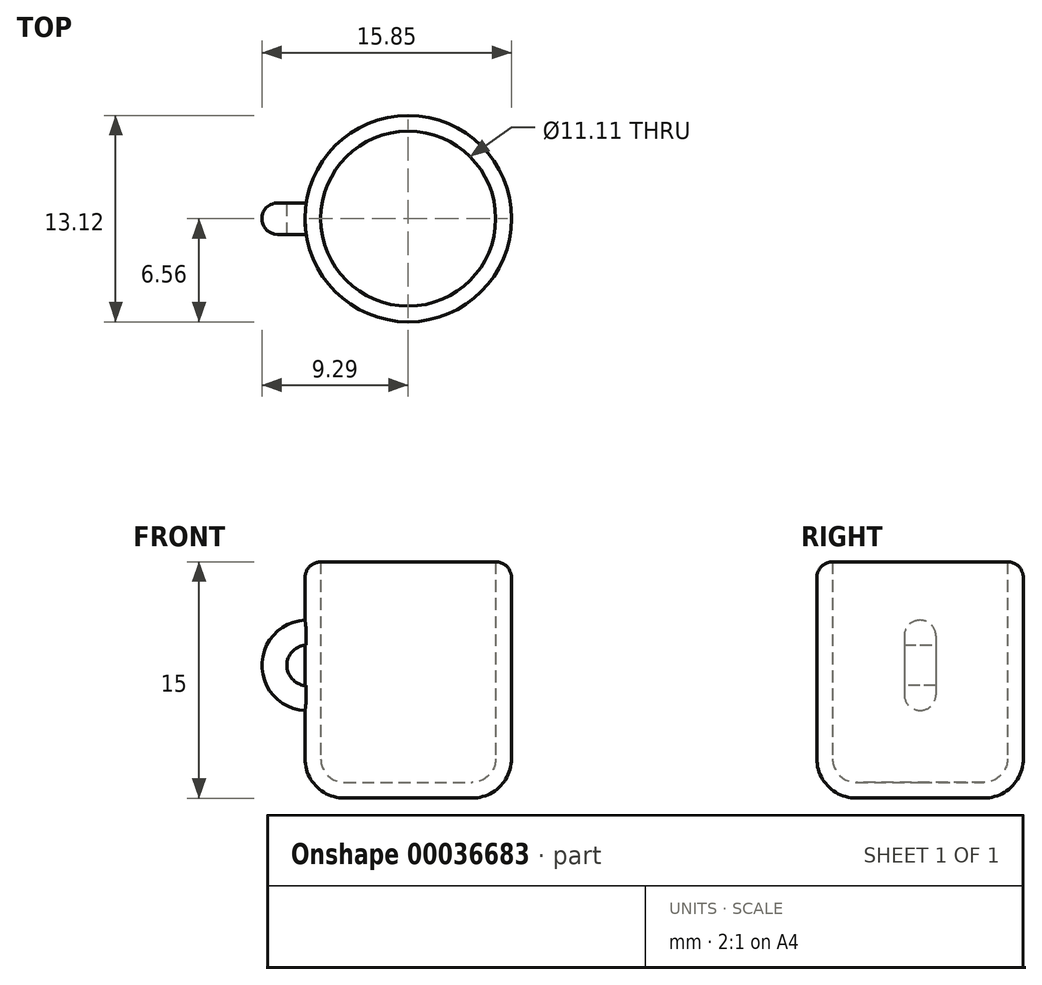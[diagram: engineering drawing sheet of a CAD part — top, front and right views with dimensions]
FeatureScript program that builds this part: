
annotation { "Feature Type Name" : "Feature", "Feature Type Description" : "" }
export const myFeature = defineFeature(function(context is Context, id is Id, definition is map)
    precondition{}
    {
        {
            var Q0;
            Q0=qCreatedBy(makeId("Front.planeOp"),FACE);
            var sketch = newSketch(context, id + "F0", { "sketchPlane" : qUnion([Q0])});
            skLineSegment(sketch, "E0", {"start": v(-6.56, 10.8) * mm, "end": v(-6.56, -1.7) * mm});
            skLineSegment(sketch, "E1", {"start": v(-4.06, -4.2) * mm, "end": v(0, -4.2) * mm});
            skLineSegment(sketch, "E2", {"start": v(0, -4.2) * mm, "end": v(0, 10.8) * mm});
            skLineSegment(sketch, "E3", {"start": v(0, 10.8) * mm, "end": v(-6.56, 10.8) * mm});
            skPoint(sketch, "E4.visualSharp", {"position": v(-6.56, -4.2) * mm});
            skArc(sketch, "E4.filletArc", {"start": v(-6.56, -1.7) * mm, "mid": v(-5.82, -3.46) * mm, "end": v(-4.06, -4.2) * mm});
            skSolve(sketch);
        }
        {
            var Q0;
            Q0=makeQuery(id+"F0.imprint","IMPRINT",FACE,{"disambiguationData":[TD([[makeQuery(id+"F0.imprint","IMPRINT",EDGE,{"derivedFrom":sQuery(id+"F0.wireOp",EDGE,"E0")}),1.0]])]});
            var Q1;
            Q1=sQuery(id+"F0.wireOp",EDGE,"E2");
            revolve(context, id + "F1", {"entities" : qUnion([Q0]), "axis" : qUnion([Q1]), "revolveType" : RevolveType.FULL});
        }
        {
            var Q0;
            Q0=makeQuery(id+"F1.opRevolve","SWEPT_FACE",FACE,{"disambiguationData":[OSD([sQuery(id+"F0.wireOp",EDGE,"E3")])]});
            shell(context, id + "F2", {"entities" : qUnion([Q0]), "thickness" : 1 * mm});
        }
        {
            var Q0;
            Q0=qCreatedBy(makeId("Front.planeOp"),FACE);
            var sketch = newSketch(context, id + "F3", { "sketchPlane" : qUnion([Q0])});
            skArc(sketch, "E5", {"start": v(-6.56, 7.1) * mm, "mid": v(-9.3, 4.24) * mm, "end": v(-6.56, 1.37) * mm});
            skArc(sketch, "E6", {"start": v(-6.56, 5.52) * mm, "mid": v(-7.7, 4.24) * mm, "end": v(-6.56, 2.96) * mm});
            skLineSegment(sketch, "E7", {"start": v(-6.56, 7.1) * mm, "end": v(-5.9, 7.14) * mm});
            skLineSegment(sketch, "E8", {"start": v(-5.9, 7.14) * mm, "end": v(-5.9, 5.5) * mm});
            skLineSegment(sketch, "E9", {"start": v(-5.9, 5.5) * mm, "end": v(-6.56, 5.52) * mm});
            skLineSegment(sketch, "E10", {"start": v(-6.56, 2.96) * mm, "end": v(-5.9, 2.89) * mm});
            skLineSegment(sketch, "E11", {"start": v(-5.9, 2.89) * mm, "end": v(-5.95, 1.41) * mm});
            skLineSegment(sketch, "E12", {"start": v(-5.95, 1.41) * mm, "end": v(-6.56, 1.37) * mm});
            skSolve(sketch);
        }
        {
            var Q0;
            Q0=makeQuery(id+"F3.imprint","IMPRINT",FACE,{"disambiguationData":[TD([[makeQuery(id+"F3.imprint","IMPRINT",EDGE,{"derivedFrom":sQuery(id+"F3.wireOp",EDGE,"E5")}),1.0]])]});
            extrude(context, id + "F4", {"entities" : qUnion([Q0]), "operationType" : NewBodyOperationType.ADD, "endBound" : BoundingType.SYMMETRIC, "depth" : 2 * mm});
        }
        {
            var Q0;
            Q0=makeQuery(id+"F4.opExtrude","CAP_EDGE",EDGE,{"disambiguationData":[OSD([sQuery(id+"F3.wireOp",EDGE,"E5")])],"isStart":false});
            var Q1;
            Q1=makeQuery(id+"F4.opExtrude","CAP_EDGE",EDGE,{"disambiguationData":[OSD([sQuery(id+"F3.wireOp",EDGE,"E5")])],"isStart":true});
            var Q2;
            Q2=makeQuery(id+"F1.opRevolve","SWEPT_EDGE",EDGE,{"disambiguationData":[OSD([sQuery(id+"F0.wireOp",EDGE,"E0"),sQuery(id+"F0.wireOp",EDGE,"E3")])]});
            fillet(context, id + "F5", {"entities" : qUnion([Q0, Q1, Q2]), "radius" : 1 * mm, "tangentPropagation" : true, "allowEdgeOverflow" : false});
        }
    });
